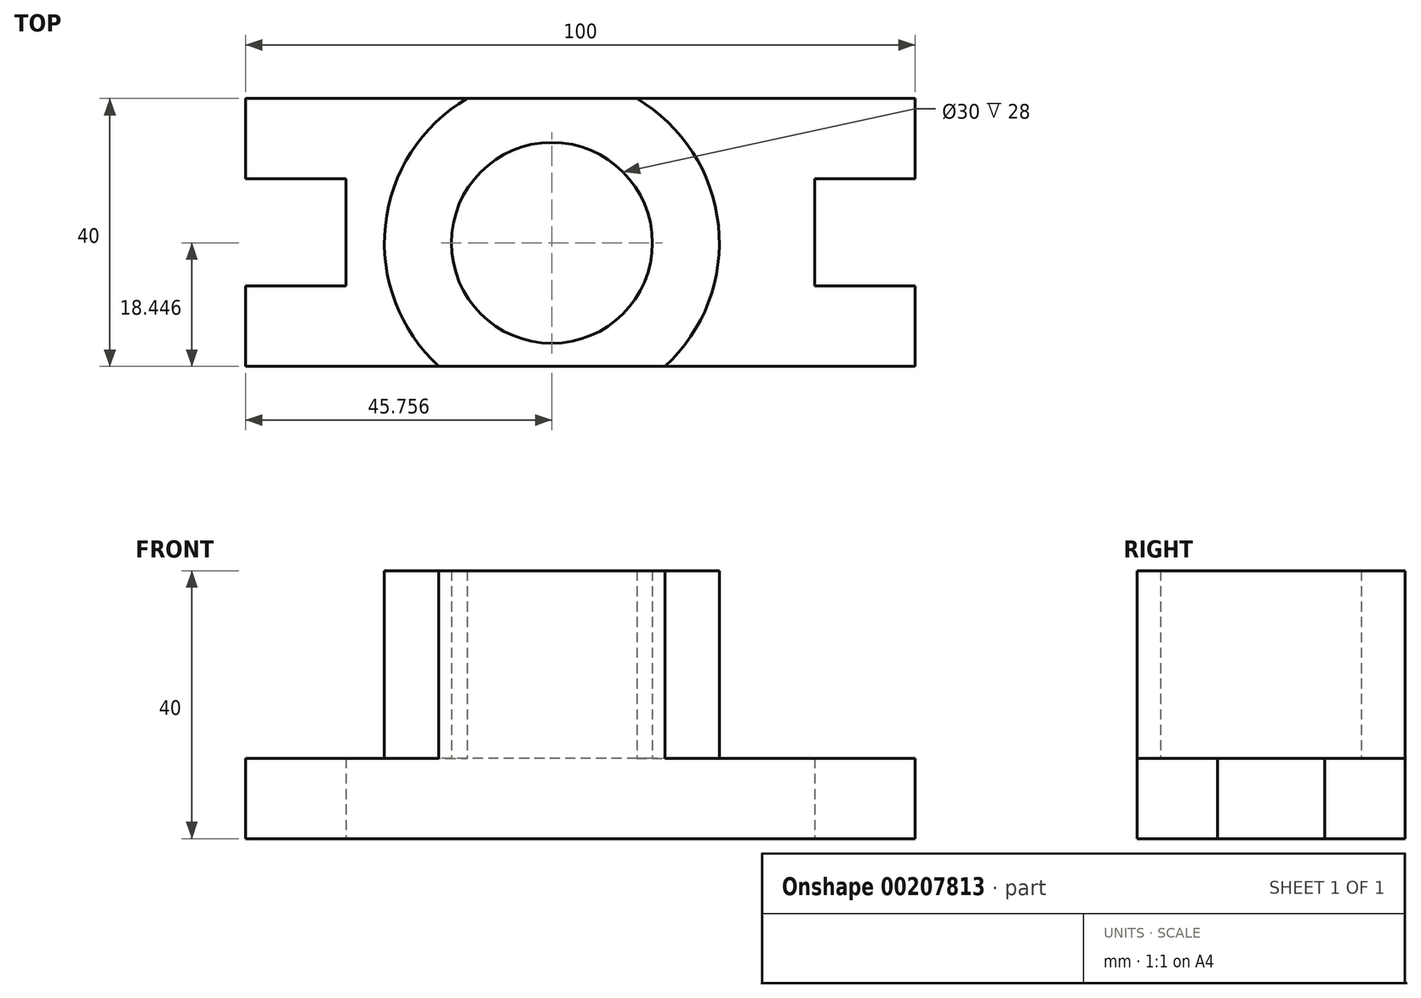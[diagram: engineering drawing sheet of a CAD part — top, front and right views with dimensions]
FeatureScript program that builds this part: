
annotation { "Feature Type Name" : "Feature", "Feature Type Description" : "" }
export const myFeature = defineFeature(function(context is Context, id is Id, definition is map)
    precondition{}
    {
        {
            var Q0;
            Q0=qCreatedBy(makeId("Top.planeOp"),FACE);
            var sketch = newSketch(context, id + "F0", { "sketchPlane" : qUnion([Q0])});
            skLineSegment(sketch, "E0.bottom", {"start": v(0, 0) * mm, "end": v(100, 0) * mm});
            skLineSegment(sketch, "E0.top", {"start": v(0, 40) * mm, "end": v(100, 40) * mm});
            skLineSegment(sketch, "E0.left", {"start": v(0, 0) * mm, "end": v(0, 40) * mm});
            skLineSegment(sketch, "E0.right", {"start": v(100, 0) * mm, "end": v(100, 40) * mm});
            skSolve(sketch);
        }
        {
            var Q0;
            Q0=makeQuery(id+"F0.imprint","IMPRINT",FACE,{"disambiguationData":[TD([[makeQuery(id+"F0.imprint","IMPRINT",EDGE,{"derivedFrom":sQuery(id+"F0.wireOp",EDGE,"E0.bottom")}),1.0]])]});
            extrude(context, id + "F1", {"entities" : qUnion([Q0]), "depth" : 12 * mm});
        }
        {
            var Q0;
            Q0=makeQuery(id+"F1.opExtrude","SWEPT_FACE",FACE,{"disambiguationData":[OSD([sQuery(id+"F0.wireOp",EDGE,"E0.right")])]});
            var sketch = newSketch(context, id + "F2", { "sketchPlane" : qUnion([Q0])});
            skLineSegment(sketch, "E1.bottom", {"start": v(12, 12) * mm, "end": v(0, 12) * mm});
            skLineSegment(sketch, "E1.top", {"start": v(12, 0) * mm, "end": v(0, 0) * mm});
            skLineSegment(sketch, "E1.left", {"start": v(12, 12) * mm, "end": v(12, 0) * mm});
            skLineSegment(sketch, "E1.right", {"start": v(0, 12) * mm, "end": v(0, 0) * mm});
            skLineSegment(sketch, "E2.bottom", {"start": v(28, 12) * mm, "end": v(40, 12) * mm});
            skLineSegment(sketch, "E2.top", {"start": v(28, 0) * mm, "end": v(40, 0) * mm});
            skLineSegment(sketch, "E2.left", {"start": v(28, 12) * mm, "end": v(28, 0) * mm});
            skLineSegment(sketch, "E2.right", {"start": v(40, 12) * mm, "end": v(40, 0) * mm});
            skLineSegment(sketch, "E3.bottom", {"start": v(12, 12) * mm, "end": v(28, 12) * mm});
            skLineSegment(sketch, "E3.top", {"start": v(12, 0) * mm, "end": v(28, 0) * mm});
            skSolve(sketch);
        }
        {
            var Q0;
            Q0=makeQuery(id+"F2.imprint","IMPRINT",FACE,{"disambiguationData":[TD([[makeQuery(id+"F2.imprint","IMPRINT",EDGE,{"derivedFrom":sQuery(id+"F2.wireOp",EDGE,"E3.bottom")}),-1.0]])]});
            extrude(context, id + "F3", {"entities" : qUnion([Q0]), "operationType" : NewBodyOperationType.REMOVE, "oppositeDirection" : true, "depth" : 15 * mm});
        }
        {
            var Q0;
            Q0=makeQuery(id+"F1.opExtrude","SWEPT_FACE",FACE,{"disambiguationData":[OSD([sQuery(id+"F0.wireOp",EDGE,"E0.left")])]});
            var sketch = newSketch(context, id + "F4", { "sketchPlane" : qUnion([Q0])});
            skLineSegment(sketch, "E4.bottom", {"start": v(-28, 12) * mm, "end": v(-40, 12) * mm});
            skLineSegment(sketch, "E4.top", {"start": v(-28, 0) * mm, "end": v(-40, 0) * mm});
            skLineSegment(sketch, "E4.left", {"start": v(-28, 12) * mm, "end": v(-28, 0) * mm});
            skLineSegment(sketch, "E4.right", {"start": v(-40, 12) * mm, "end": v(-40, 0) * mm});
            skLineSegment(sketch, "E5.bottom", {"start": v(0, 12) * mm, "end": v(-12, 12) * mm});
            skLineSegment(sketch, "E5.top", {"start": v(0, 0) * mm, "end": v(-12, 0) * mm});
            skLineSegment(sketch, "E5.left", {"start": v(0, 12) * mm, "end": v(0, 0) * mm});
            skLineSegment(sketch, "E5.right", {"start": v(-12, 12) * mm, "end": v(-12, 0) * mm});
            skLineSegment(sketch, "E6.bottom", {"start": v(-28, 12) * mm, "end": v(-12, 12) * mm});
            skLineSegment(sketch, "E6.top", {"start": v(-28, 0) * mm, "end": v(-12, 0) * mm});
            skSolve(sketch);
        }
        {
            var Q0;
            Q0=makeQuery(id+"F4.imprint","IMPRINT",FACE,{"disambiguationData":[TD([[makeQuery(id+"F4.imprint","IMPRINT",EDGE,{"derivedFrom":sQuery(id+"F4.wireOp",EDGE,"E6.bottom")}),1.0]])]});
            extrude(context, id + "F5", {"entities" : qUnion([Q0]), "operationType" : NewBodyOperationType.REMOVE, "oppositeDirection" : true, "depth" : 15 * mm});
        }
        {
            var Q0;
            Q0=makeQuery(id+"F1.opExtrude","CAP_FACE",FACE,{"disambiguationData":[OSD([sQuery(id+"F0.wireOp",EDGE,"E0.bottom"),sQuery(id+"F0.wireOp",EDGE,"E0.top"),sQuery(id+"F0.wireOp",EDGE,"E0.left"),sQuery(id+"F0.wireOp",EDGE,"E0.right")])],"isStart":true});
            var sketch = newSketch(context, id + "F6", { "sketchPlane" : qUnion([Q0])});
            skCircle(sketch, "E7", {"center": v(45.76, -18.45) * mm, "radius": 25 * mm});
            skCircle(sketch, "E8", {"center": v(45.76, -18.45) * mm, "radius": 15 * mm});
            skSolve(sketch);
        }
        {
            var Q0;
            Q0=makeQuery(id+"F6.imprint","IMPRINT",FACE,{"disambiguationData":[TD([[makeQuery(id+"F6.imprint","IMPRINT",EDGE,{"derivedFrom":sQuery(id+"F6.wireOp",EDGE,"E8")}),-1.0]])]});
            extrude(context, id + "F7", {"entities" : qUnion([Q0]), "operationType" : NewBodyOperationType.ADD, "oppositeDirection" : true, "depth" : 40 * mm});
        }
    });
